# Revit family: PlumbingFixture_Valve_AVG_PLV20C
name_source: partatom
category: Pipe Accessories
revit_build: Autodesk Revit 2017 (Build: 20190508_0315(x64)
units: mm (PartAtom-declared; Revit-internal decimal feet)

## family parameters
Always vertical = Yes
Cut with Voids When Loaded = No
OmniClass Number = 23.60.30.11.14
OmniClass Title = Pipework Fittings
Part Type = Valve - Breaks Into
Round Connector Dimension = Use Radius
Shared = No
Work Plane-Based = No

## types (1)
- Type 1
    Bypass_Size = 0 mm  [stored 0 ft]
    CW Connection = No
    CWFU = 0
    Default Elevation = 0 mm  [stored 0 ft]
    Description = Pressure Limiting Valve assembly. 20mm compression connection.Settable for 3 outlet pressures - 350, 500, 600 kPa
    Factory_Set_Pressure (kPa) = 500
    HW Connection = No
    HWFU = 0
    Hot_Water_Supply_Temp (°C ) = Max 80
    Inlet_Size = 20 mm  [stored 0.0656168 ft]
    Inlet_Size Radius = 10 mm  [stored 0.0328084 ft]
    Inlet_Type = Compression
    Loss Method = Not Defined
    Manufacturer = Australian Valve Group
    Max_Flow_Rate (l/min) = 130
    Max_Supply_Pressure_Static (kPa) = 1800
    Outlet_Pressure_Range (kPa) = 350,500 or 600
    Outlet_Size = 20 mm  [stored 0.0656168 ft]
    Outlet_Size Radius = 10 mm  [stored 0.0328084 ft]
    Outlet_Type = Compression
    PlumbingMaterial_ANZRS = <By Category>
    Product_Type = PLV20C-TRISET
    Set_Pressure (kPa) = 600
    Specify_Host = Face
    URL = https://www.avg.net.au
    Valve_Model = PLV20C
    Vent Connection = No
    WFU = 0
    Waste Connection = No

note: [stored X ft] marks values corroborated as IEEE doubles in the binary element streams (Revit-internal decimal feet)

## geometry (parser evidence)
native form markers: Sweep x8
no freeform markers — native parametric forms only
